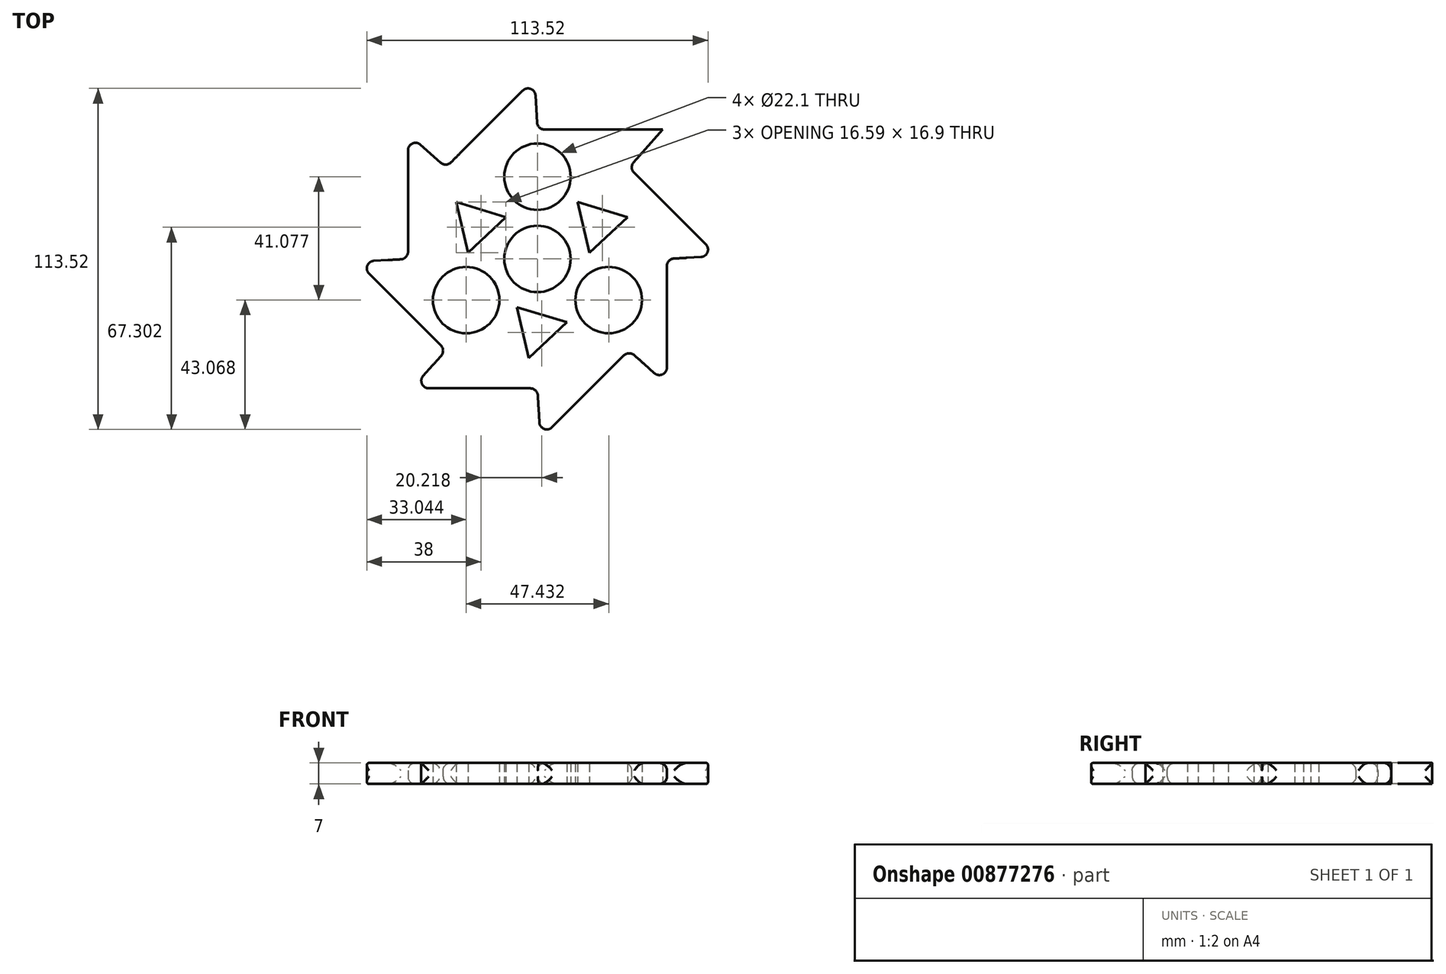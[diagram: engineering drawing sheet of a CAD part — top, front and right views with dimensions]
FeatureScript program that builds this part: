
annotation { "Feature Type Name" : "Feature", "Feature Type Description" : "" }
export const myFeature = defineFeature(function(context is Context, id is Id, definition is map)
    precondition{}
    {
        {
            var Q0;
            Q0=qCreatedBy(makeId("Top.planeOp"),FACE);
            var sketch = newSketch(context, id + "F0", { "sketchPlane" : qUnion([Q0])});
            skCircle(sketch, "E0", {"center": v(0, 0) * mm, "radius": 11.05 * mm});
            skArc(sketch, "E1", {"start": v(-1.58, -13.46) * mm, "mid": v(0, -13.55) * mm, "end": v(1.58, -13.46) * mm});
            skCircle(sketch, "E2", {"center": v(0, 27.38) * mm, "radius": 11.05 * mm});
            skCircle(sketch, "E3.1.1", {"center": v(-23.72, -13.7) * mm, "radius": 11.05 * mm});
            skCircle(sketch, "E3.2.1", {"center": v(23.72, -13.7) * mm, "radius": 11.05 * mm});
            skCircle(sketch, "E4.cCircle", {"center": v(-20.22, 11.67) * mm, "radius": 10.01 * mm, "construction": true});
            skLineSegment(sketch, "E4.0", {"start": v(-10.46, 13.94) * mm, "end": v(-23.14, 2.1) * mm});
            skLineSegment(sketch, "E4.1", {"start": v(-23.14, 2.1) * mm, "end": v(-27.06, 18.99) * mm});
            skLineSegment(sketch, "E4.2", {"start": v(-27.06, 18.99) * mm, "end": v(-10.46, 13.94) * mm});
            skLineSegment(sketch, "E5.1.0", {"start": v(-2.92, -32.93) * mm, "end": v(-6.84, -16.03) * mm});
            skLineSegment(sketch, "E5.1.1", {"start": v(9.75, -21.08) * mm, "end": v(-2.92, -32.93) * mm});
            skLineSegment(sketch, "E5.1.2", {"start": v(-6.84, -16.03) * mm, "end": v(9.75, -21.08) * mm});
            skCircle(sketch, "E5.1.3", {"center": v(0, -23.35) * mm, "radius": 10.01 * mm, "construction": true});
            skLineSegment(sketch, "E5.2.0", {"start": v(29.97, 13.94) * mm, "end": v(17.3, 2.1) * mm});
            skLineSegment(sketch, "E5.2.1", {"start": v(13.38, 18.99) * mm, "end": v(29.97, 13.94) * mm});
            skLineSegment(sketch, "E5.2.2", {"start": v(17.3, 2.1) * mm, "end": v(13.38, 18.99) * mm});
            skCircle(sketch, "E5.2.3", {"center": v(20.22, 11.67) * mm, "radius": 10.01 * mm, "construction": true});
            skArc(sketch, "E6.trimOffspring", {"start": v(-10.87, 8.1) * mm, "mid": v(-11.73, 6.77) * mm, "end": v(-12.44, 5.36) * mm});
            skArc(sketch, "E7.trimOffspring", {"start": v(12.44, 5.36) * mm, "mid": v(11.73, 6.78) * mm, "end": v(10.87, 8.1) * mm});
            skLineSegment(sketch, "E8", {"start": v(0, 42.19) * mm, "end": v(0, -38.93) * mm});
            skCircle(sketch, "E9.cCircle", {"center": v(0, 0) * mm, "radius": 43.08 * mm, "construction": true});
            skLineSegment(sketch, "E9.0", {"start": v(0, -43.08) * mm, "end": v(-30.46, -30.46) * mm});
            skLineSegment(sketch, "E9.1", {"start": v(-30.46, -30.46) * mm, "end": v(-43.08, 0) * mm});
            skLineSegment(sketch, "E9.2", {"start": v(-43.08, 0) * mm, "end": v(-30.46, 30.46) * mm});
            skLineSegment(sketch, "E9.3", {"start": v(-30.46, 30.46) * mm, "end": v(0, 43.08) * mm});
            skLineSegment(sketch, "E9.4", {"start": v(0, 43.08) * mm, "end": v(30.46, 30.46) * mm});
            skLineSegment(sketch, "E9.5", {"start": v(30.46, 30.46) * mm, "end": v(43.08, 0) * mm});
            skLineSegment(sketch, "E9.6", {"start": v(43.08, 0) * mm, "end": v(30.46, -30.46) * mm});
            skLineSegment(sketch, "E9.7", {"start": v(30.46, -30.46) * mm, "end": v(0, -43.08) * mm});
            skLineSegment(sketch, "E10", {"start": v(0, -43.08) * mm, "end": v(-41.74, -43.08) * mm});
            skLineSegment(sketch, "E11", {"start": v(-41.74, -43.08) * mm, "end": v(-30.46, -30.46) * mm});
            skLineSegment(sketch, "E12.1.0", {"start": v(30.46, -30.46) * mm, "end": v(0.94, -59.98) * mm});
            skLineSegment(sketch, "E12.1.1", {"start": v(0.94, -59.98) * mm, "end": v(0, -43.08) * mm});
            skLineSegment(sketch, "E12.2.0", {"start": v(43.08, 0) * mm, "end": v(43.08, -41.74) * mm});
            skLineSegment(sketch, "E12.2.1", {"start": v(43.08, -41.74) * mm, "end": v(30.46, -30.46) * mm});
            skLineSegment(sketch, "E12.3.0", {"start": v(30.46, 30.46) * mm, "end": v(59.98, 0.94) * mm});
            skLineSegment(sketch, "E12.3.1", {"start": v(59.98, 0.94) * mm, "end": v(43.08, 0) * mm});
            skLineSegment(sketch, "E12.4.0", {"start": v(0, 43.08) * mm, "end": v(41.74, 43.08) * mm});
            skLineSegment(sketch, "E12.4.1", {"start": v(41.74, 43.08) * mm, "end": v(30.46, 30.46) * mm});
            skLineSegment(sketch, "E12.5.0", {"start": v(-30.46, 30.46) * mm, "end": v(-0.94, 59.98) * mm});
            skLineSegment(sketch, "E12.5.1", {"start": v(-0.94, 59.98) * mm, "end": v(0, 43.08) * mm});
            skLineSegment(sketch, "E12.6.0", {"start": v(-43.08, 0) * mm, "end": v(-43.08, 41.74) * mm});
            skLineSegment(sketch, "E12.6.1", {"start": v(-43.08, 41.74) * mm, "end": v(-30.46, 30.46) * mm});
            skLineSegment(sketch, "E12.7.0", {"start": v(-30.46, -30.46) * mm, "end": v(-59.98, -0.94) * mm});
            skLineSegment(sketch, "E12.7.1", {"start": v(-59.98, -0.94) * mm, "end": v(-43.08, 0) * mm});
            skSolve(sketch);
        }
        {
            var Q0;
            Q0=makeQuery(id+"F0.imprint","IMPRINT",FACE,{"disambiguationData":[TD([[makeQuery(id+"F0.imprint","IMPRINT",EDGE,{"derivedFrom":sQuery(id+"F0.wireOp",EDGE,"E3.1.1")}),-1.0]])]});
            var Q1;
            Q1=makeQuery(id+"F0.imprint","IMPRINT",FACE,{"disambiguationData":[TD([[makeQuery(id+"F0.imprint","IMPRINT",EDGE,{"derivedFrom":sQuery(id+"F0.wireOp",EDGE,"E9.3")}),1.0]])]});
            var Q2;
            Q2=makeQuery(id+"F0.imprint","IMPRINT",FACE,{"disambiguationData":[TD([[makeQuery(id+"F0.imprint","IMPRINT",EDGE,{"derivedFrom":sQuery(id+"F0.wireOp",EDGE,"E9.2")}),1.0]])]});
            var Q3;
            Q3=makeQuery(id+"F0.imprint","IMPRINT",FACE,{"disambiguationData":[TD([[makeQuery(id+"F0.imprint","IMPRINT",EDGE,{"derivedFrom":sQuery(id+"F0.wireOp",EDGE,"E9.1")}),1.0]])]});
            var Q4;
            Q4=makeQuery(id+"F0.imprint","IMPRINT",FACE,{"disambiguationData":[TD([[makeQuery(id+"F0.imprint","IMPRINT",EDGE,{"derivedFrom":sQuery(id+"F0.wireOp",EDGE,"E9.4")}),1.0]])]});
            var Q5;
            Q5=makeQuery(id+"F0.imprint","IMPRINT",FACE,{"disambiguationData":[TD([[makeQuery(id+"F0.imprint","IMPRINT",EDGE,{"derivedFrom":sQuery(id+"F0.wireOp",EDGE,"E9.0")}),1.0]])]});
            var Q6;
            Q6=makeQuery(id+"F0.imprint","IMPRINT",FACE,{"disambiguationData":[TD([[makeQuery(id+"F0.imprint","IMPRINT",EDGE,{"derivedFrom":sQuery(id+"F0.wireOp",EDGE,"E9.7")}),1.0]])]});
            var Q7;
            Q7=makeQuery(id+"F0.imprint","IMPRINT",FACE,{"disambiguationData":[TD([[makeQuery(id+"F0.imprint","IMPRINT",EDGE,{"derivedFrom":sQuery(id+"F0.wireOp",EDGE,"E9.6")}),1.0]])]});
            var Q8;
            Q8=makeQuery(id+"F0.imprint","IMPRINT",FACE,{"disambiguationData":[TD([[makeQuery(id+"F0.imprint","IMPRINT",EDGE,{"derivedFrom":sQuery(id+"F0.wireOp",EDGE,"E9.5")}),1.0]])]});
            extrude(context, id + "F1", {"entities" : qUnion([Q0, Q1, Q2, Q3, Q4, Q5, Q6, Q7, Q8]), "depth" : 7 * mm, "offsetDistance" : 25 * mm});
        }
        {
            var Q0;
            Q0=makeQuery(id+"F1.opExtrude","SWEPT_FACE",FACE,{"disambiguationData":[OSD([sQuery(id+"F0.wireOp",EDGE,"E12.6.1")])]});
            var Q1;
            Q1=makeQuery(id+"F1.opExtrude","SWEPT_FACE",FACE,{"disambiguationData":[OSD([sQuery(id+"F0.wireOp",EDGE,"E12.5.1")])]});
            var Q2;
            Q2=makeQuery(id+"F1.opExtrude","SWEPT_FACE",FACE,{"disambiguationData":[OSD([sQuery(id+"F0.wireOp",EDGE,"E12.3.0")])]});
            var Q3;
            Q3=makeQuery(id+"F1.opExtrude","SWEPT_FACE",FACE,{"disambiguationData":[OSD([sQuery(id+"F0.wireOp",EDGE,"E12.2.0")])]});
            var Q4;
            Q4=makeQuery(id+"F1.opExtrude","SWEPT_FACE",FACE,{"disambiguationData":[OSD([sQuery(id+"F0.wireOp",EDGE,"E12.1.0")])]});
            var Q5;
            Q5=makeQuery(id+"F1.opExtrude","SWEPT_FACE",FACE,{"disambiguationData":[OSD([sQuery(id+"F0.wireOp",EDGE,"E10")])]});
            var Q6;
            Q6=makeQuery(id+"F1.opExtrude","SWEPT_FACE",FACE,{"disambiguationData":[OSD([sQuery(id+"F0.wireOp",EDGE,"E12.7.0")])]});
            var Q7;
            Q7=makeQuery(id+"F1.opExtrude","SWEPT_FACE",FACE,{"disambiguationData":[OSD([sQuery(id+"F0.wireOp",EDGE,"E12.6.0")])]});
            fillet(context, id + "F2", {"entities" : qUnion([Q0, Q1, Q2, Q3, Q4, Q5, Q6, Q7]), "radius" : 2.5 * mm, "tangentPropagation" : true, "allowEdgeOverflow" : false});
        }
    });
